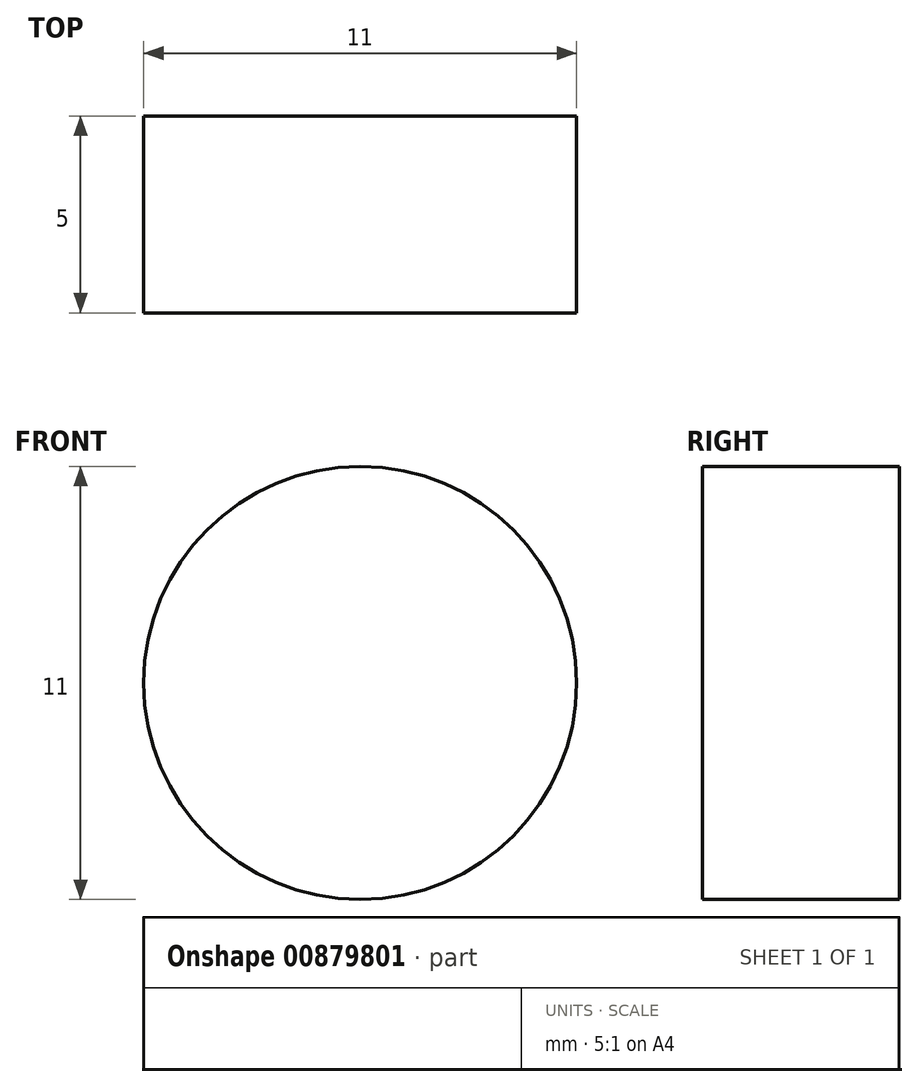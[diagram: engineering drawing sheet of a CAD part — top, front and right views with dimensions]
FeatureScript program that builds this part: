
annotation { "Feature Type Name" : "Feature", "Feature Type Description" : "" }
export const myFeature = defineFeature(function(context is Context, id is Id, definition is map)
    precondition{}
    {
        {
            var Q0;
            Q0=qCreatedBy(makeId("Right.planeOp"),FACE);
            var sketch = newSketch(context, id + "F0", { "sketchPlane" : qUnion([Q0])});
            skLineSegment(sketch, "E0", {"start": v(-25, 25) * mm, "end": v(-25, 0) * mm});
            skLineSegment(sketch, "E1", {"start": v(-25, 0) * mm, "end": v(0, 0) * mm});
            skLineSegment(sketch, "E2", {"start": v(0, 0) * mm, "end": v(0, 5) * mm});
            skLineSegment(sketch, "E3", {"start": v(0, 5) * mm, "end": v(-20, 5) * mm});
            skLineSegment(sketch, "E4", {"start": v(-20, 5) * mm, "end": v(-20, 25) * mm});
            skLineSegment(sketch, "E5", {"start": v(-25, 25) * mm, "end": v(-20, 25) * mm});
            skSolve(sketch);
        }
        {
            var Q0;
            Q0=makeQuery(id+"F0.imprint","IMPRINT",FACE,{"disambiguationData":[TD([[makeQuery(id+"F0.imprint","IMPRINT",EDGE,{"derivedFrom":sQuery(id+"F0.wireOp",EDGE,"E0")}),1.0]])]});
            extrude(context, id + "F1", {"entities" : qUnion([Q0]), "depth" : 278 * mm, "offsetDistance" : 25 * mm, "symmetric" : true});
        }
        {
            var Q0;
            Q0=makeQuery(id+"F1.opExtrude","SWEPT_FACE",FACE,{"disambiguationData":[OSD([sQuery(id+"F0.wireOp",EDGE,"E0")])]});
            var sketch = newSketch(context, id + "F2", { "sketchPlane" : qUnion([Q0])});
            skCircle(sketch, "E6", {"center": v(129, 15) * mm, "radius": 5.5 * mm});
            skCircle(sketch, "E7.MirrorC", {"center": v(-129, 15) * mm, "radius": 5.5 * mm});
            skSolve(sketch);
        }
        {
            var Q0;
            Q0=makeQuery(id+"F2.imprint","IMPRINT",FACE,{"disambiguationData":[TD([[makeQuery(id+"F2.imprint","IMPRINT",EDGE,{"derivedFrom":sQuery(id+"F2.wireOp",EDGE,"E6")}),1.0]])]});
            var Q1;
            Q1=makeQuery(id+"F2.imprint","IMPRINT",FACE,{"disambiguationData":[TD([[makeQuery(id+"F2.imprint","IMPRINT",EDGE,{"derivedFrom":sQuery(id+"F2.wireOp",EDGE,"E7.MirrorC")}),-1.0]])]});
            extrude(context, id + "F3", {"entities" : qUnion([Q0, Q1]), "operationType" : NewBodyOperationType.REMOVE, "endBound" : BoundingType.THROUGH_ALL, "oppositeDirection" : true, "depth" : 25 * mm, "offsetDistance" : 25 * mm});
        }
    });
